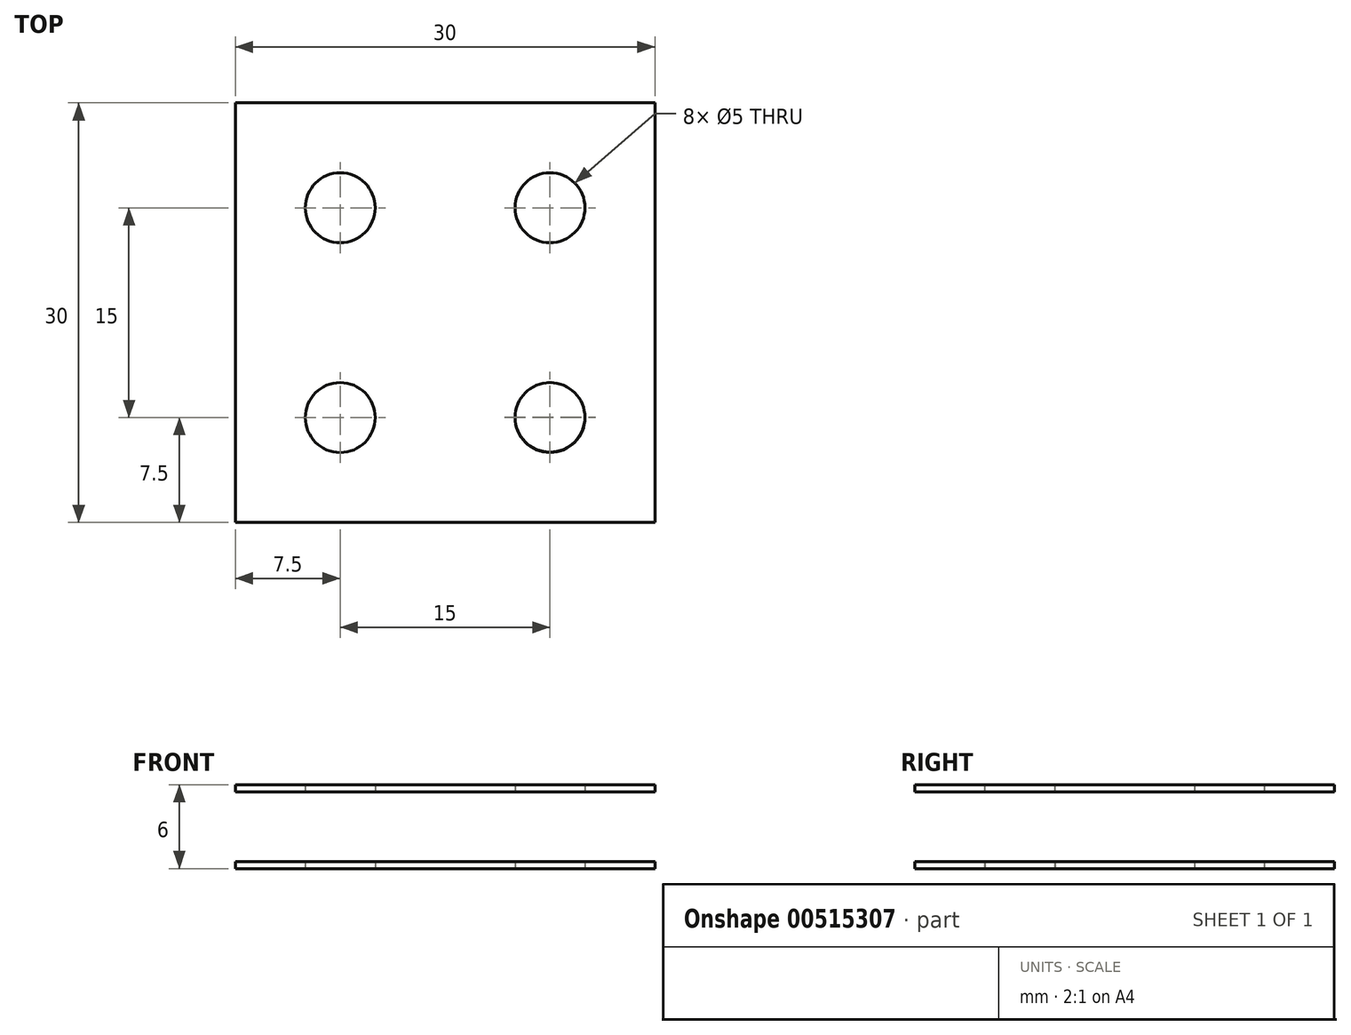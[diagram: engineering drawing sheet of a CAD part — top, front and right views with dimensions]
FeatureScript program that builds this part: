
annotation { "Feature Type Name" : "Feature", "Feature Type Description" : "" }
export const myFeature = defineFeature(function(context is Context, id is Id, definition is map)
    precondition{}
    {
        {
            var Q0;
            Q0=qCreatedBy(makeId("Top.planeOp"),FACE);
            var sketch = newSketch(context, id + "F0", { "sketchPlane" : qUnion([Q0])});
            skLineSegment(sketch, "E0.bottom", {"start": v(-15, 15) * mm, "end": v(15, 15) * mm});
            skLineSegment(sketch, "E0.top", {"start": v(-15, -15) * mm, "end": v(15, -15) * mm});
            skLineSegment(sketch, "E0.left", {"start": v(-15, 15) * mm, "end": v(-15, -15) * mm});
            skLineSegment(sketch, "E0.right", {"start": v(15, 15) * mm, "end": v(15, -15) * mm});
            skCircle(sketch, "E1", {"center": v(-7.5, 7.5) * mm, "radius": 2.5 * mm});
            skCircle(sketch, "E2", {"center": v(7.5, 7.5) * mm, "radius": 2.5 * mm});
            skCircle(sketch, "E3", {"center": v(7.5, -7.47) * mm, "radius": 2.5 * mm});
            skCircle(sketch, "E4", {"center": v(-7.5, -7.5) * mm, "radius": 2.5 * mm});
            skSolve(sketch);
        }
        {
            var Q0;
            Q0 = qSketchRegion(id + "F0", true);
            extrude(context, id + "F1", {"entities" : qUnion([Q0]), "depth" : .5 * mm, "offsetDistance" : 25 * mm});
        }
        {
            var Q0;
            Q0=makeQuery(id+"F1.opExtrude","CAP_FACE",FACE,{"disambiguationData":[OSD([sQuery(id+"F0.wireOp",EDGE,"E0.bottom"),sQuery(id+"F0.wireOp",EDGE,"E0.top"),sQuery(id+"F0.wireOp",EDGE,"E0.left"),sQuery(id+"F0.wireOp",EDGE,"E0.right"),sQuery(id+"F0.wireOp",EDGE,"E1"),sQuery(id+"F0.wireOp",EDGE,"E2"),sQuery(id+"F0.wireOp",EDGE,"E3"),sQuery(id+"F0.wireOp",EDGE,"E4")])],"isStart":false});
            cPlane(context, id + "F2", {"entities" : qUnion([Q0]), "cplaneType" : CPlaneType.OFFSET, "offset" : 5 * mm, "width" : 150 * mm, "height" : 150 * mm});
        }
        {
            var Q0;
            Q0=qCreatedBy(id+"F2.planeOp",FACE);
            var sketch = newSketch(context, id + "F3", { "sketchPlane" : qUnion([Q0])});
            skLineSegment(sketch, "E5.bottom", {"start": v(-15, 15) * mm, "end": v(15, 15) * mm});
            skLineSegment(sketch, "E5.top", {"start": v(-15, -15) * mm, "end": v(15, -15) * mm});
            skLineSegment(sketch, "E5.left", {"start": v(-15, 15) * mm, "end": v(-15, -15) * mm});
            skLineSegment(sketch, "E5.right", {"start": v(15, 15) * mm, "end": v(15, -15) * mm});
            skCircle(sketch, "E6", {"center": v(-7.5, 7.5) * mm, "radius": 2.5 * mm});
            skCircle(sketch, "E7", {"center": v(7.5, 7.5) * mm, "radius": 2.5 * mm});
            skCircle(sketch, "E8", {"center": v(7.5, -7.5) * mm, "radius": 2.5 * mm});
            skCircle(sketch, "E9", {"center": v(-7.5, -7.5) * mm, "radius": 2.5 * mm});
            skSolve(sketch);
        }
        {
            var Q0;
            Q0 = qSketchRegion(id + "F3", true);
            extrude(context, id + "F4", {"entities" : qUnion([Q0]), "depth" : .5 * mm, "offsetDistance" : 25 * mm});
        }
    });
